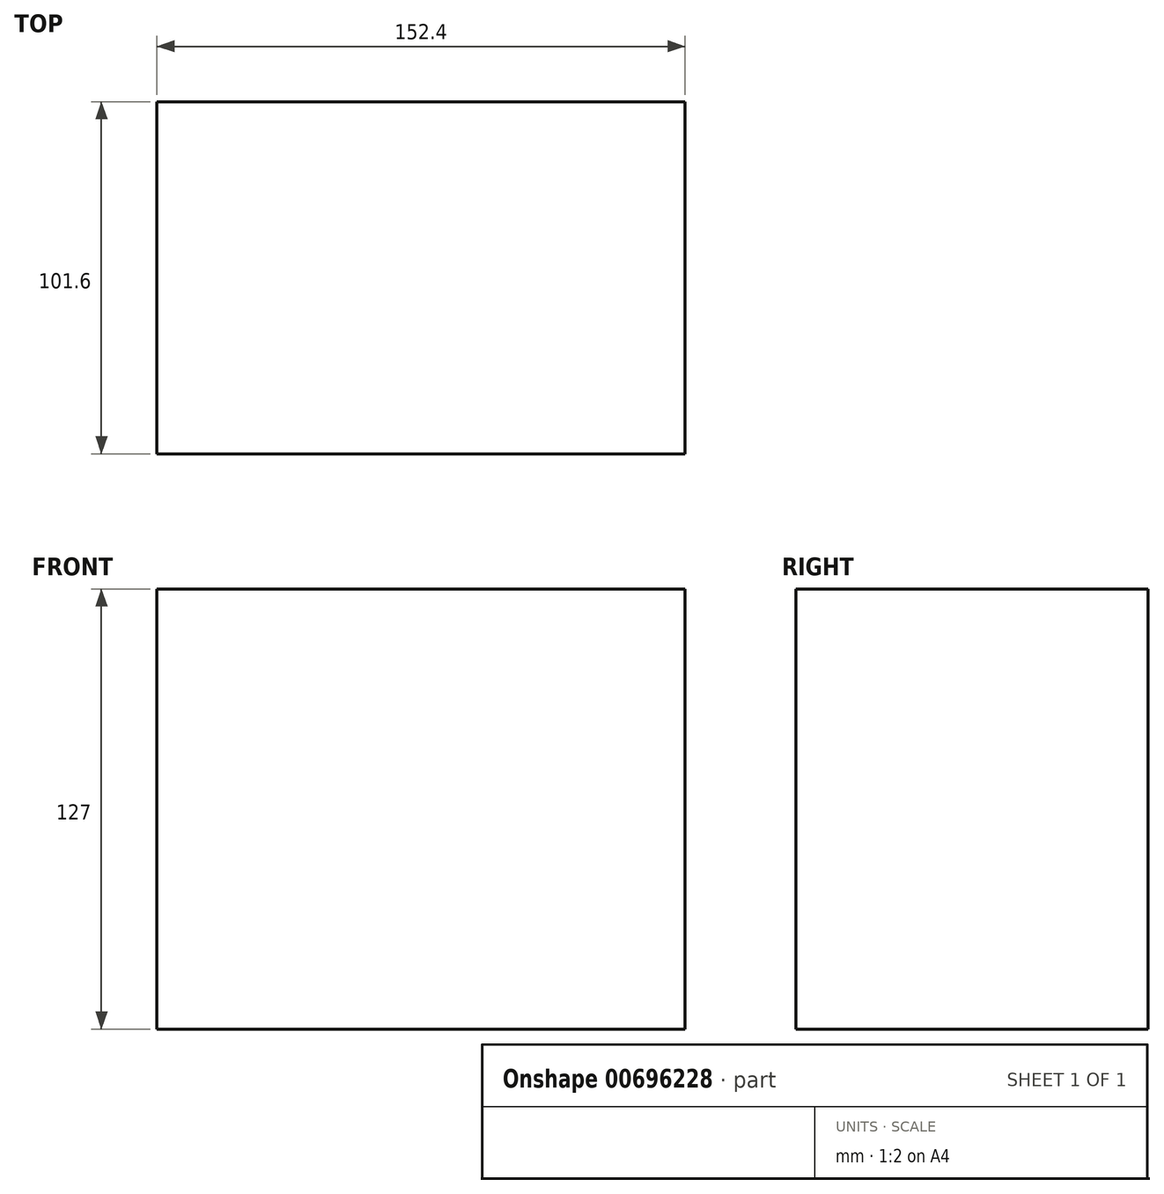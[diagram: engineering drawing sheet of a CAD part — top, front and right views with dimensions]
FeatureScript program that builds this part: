
annotation { "Feature Type Name" : "Feature", "Feature Type Description" : "" }
export const myFeature = defineFeature(function(context is Context, id is Id, definition is map)
    precondition{}
    {
        {
            var Q0;
            Q0=qCreatedBy(makeId("Front.planeOp"),FACE);
            var sketch = newSketch(context, id + "F0", { "sketchPlane" : qUnion([Q0])});
            skLineSegment(sketch, "E0", {"start": v(0, 0) * mm, "end": v(152.4, 0) * mm});
            skLineSegment(sketch, "E1", {"start": v(0, 0) * mm, "end": v(0, 127) * mm});
            skLineSegment(sketch, "E2", {"start": v(152.4, 0) * mm, "end": v(152.4, 127) * mm});
            skLineSegment(sketch, "E3", {"start": v(152.4, 127) * mm, "end": v(0, 127) * mm});
            skSolve(sketch);
        }
        {
            var Q0;
            Q0=makeQuery(id+"F0.imprint","IMPRINT",FACE,{"disambiguationData":[TD([[makeQuery(id+"F0.imprint","IMPRINT",EDGE,{"derivedFrom":sQuery(id+"F0.wireOp",EDGE,"E0")}),1.0]])]});
            extrude(context, id + "F1", {"entities" : qUnion([Q0]), "depth" : 101.6 * mm, "offsetDistance" : 25.4 * mm});
        }
    });
